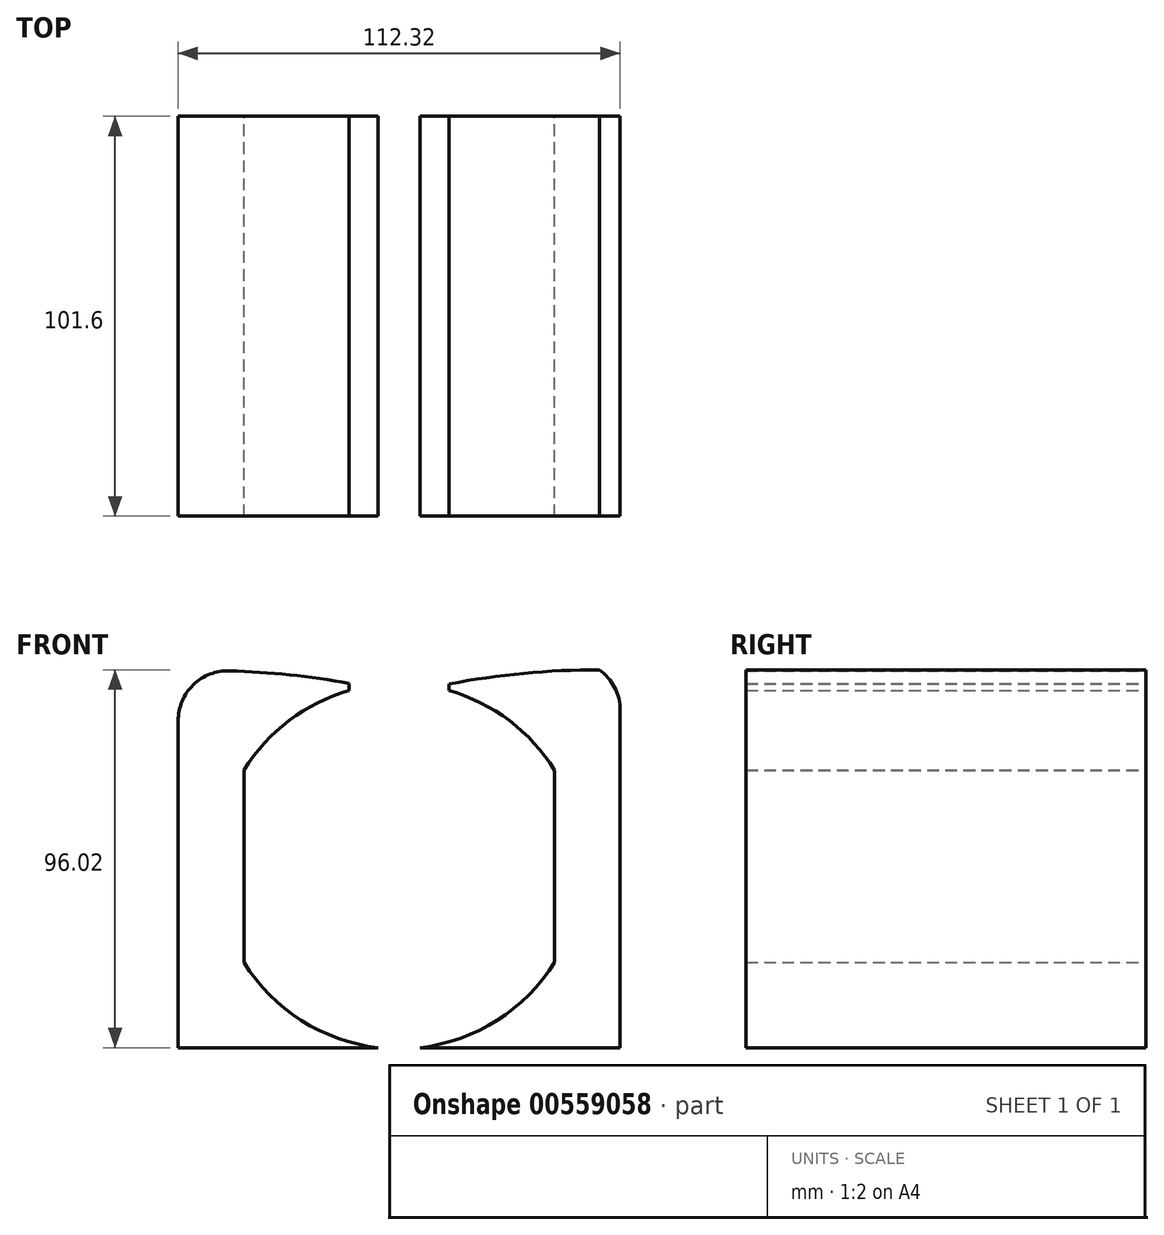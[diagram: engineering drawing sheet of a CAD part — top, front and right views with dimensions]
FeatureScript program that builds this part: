
annotation { "Feature Type Name" : "Feature", "Feature Type Description" : "" }
export const myFeature = defineFeature(function(context is Context, id is Id, definition is map)
    precondition{}
    {
        {
            var Q0;
            Q0=qCreatedBy(makeId("Front.planeOp"),FACE);
            var sketch = newSketch(context, id + "F0", { "sketchPlane" : qUnion([Q0])});
            skLineSegment(sketch, "E0.top", {"start": v(-56.16, -53.27) * mm, "end": v(-5.36, -53.27) * mm});
            skLineSegment(sketch, "E0.left", {"start": v(-56.16, 29.78) * mm, "end": v(-56.16, -53.27) * mm});
            skLineSegment(sketch, "E0.right", {"start": v(-12.7, 39.28) * mm, "end": v(-12.7, 37.44) * mm});
            skLineSegment(sketch, "E1.top", {"start": v(5.36, -53.27) * mm, "end": v(56.16, -53.27) * mm});
            skLineSegment(sketch, "E1.left", {"start": v(12.7, 39.14) * mm, "end": v(12.7, 37.44) * mm});
            skLineSegment(sketch, "E1.right", {"start": v(56.16, 32.42) * mm, "end": v(56.16, -53.27) * mm});
            skPoint(sketch, "E2.visualSharp", {"position": v(-56.16, 42.06) * mm});
            skArc(sketch, "E2.filletArc", {"start": v(-43.08, 42.48) * mm, "mid": v(-52.3, 38.9) * mm, "end": v(-56.16, 29.78) * mm});
            skPoint(sketch, "E3.visualSharp", {"position": v(56.16, 42.06) * mm});
            skArc(sketch, "E3.filletArc", {"start": v(56.16, 32.42) * mm, "mid": v(54.75, 38.23) * mm, "end": v(50.83, 42.75) * mm});
            skArc(sketch, "E4", {"start": v(5.36, -53.27) * mm, "mid": v(24.9, -46.34) * mm, "end": v(39.46, -31.58) * mm});
            skArc(sketch, "E5", {"start": v(39.46, 17.21) * mm, "mid": v(27.97, 29.83) * mm, "end": v(12.7, 37.44) * mm});
            skArc(sketch, "E6.trimOffspring", {"start": v(-12.7, 37.44) * mm, "mid": v(-27.95, 29.85) * mm, "end": v(-39.43, 17.27) * mm});
            skLineSegment(sketch, "E7", {"start": v(-39.43, 17.27) * mm, "end": v(-39.43, -31.64) * mm});
            skLineSegment(sketch, "E8", {"start": v(39.46, 17.21) * mm, "end": v(39.46, -31.58) * mm});
            skArc(sketch, "E9.trimOffspring", {"start": v(-39.43, -31.64) * mm, "mid": v(-24.87, -46.35) * mm, "end": v(-5.36, -53.27) * mm});
            skPoint(sketch, "E10.orphan", {"position": v(45.84, 0) * mm});
            skArc(sketch, "E11", {"start": v(-12.7, 39.28) * mm, "mid": v(-27.83, 41.45) * mm, "end": v(-43.08, 42.48) * mm});
            skArc(sketch, "E12", {"start": v(50.83, 42.75) * mm, "mid": v(31.68, 41.85) * mm, "end": v(12.7, 39.14) * mm});
            skPoint(sketch, "E13.orphan", {"position": v(-12.7, 42.06) * mm});
            skPoint(sketch, "E14.orphan", {"position": v(-43.08, 39.86) * mm});
            skPoint(sketch, "E15.end.orphan", {"position": v(50.83, 39.68) * mm});
            skSolve(sketch);
        }
        {
            var Q0;
            Q0=makeQuery(id+"F0.imprint","IMPRINT",FACE,{"disambiguationData":[TD([[makeQuery(id+"F0.imprint","IMPRINT",EDGE,{"derivedFrom":sQuery(id+"F0.wireOp",EDGE,"E0.top")}),1.0]])]});
            var Q1;
            Q1=makeQuery(id+"F0.imprint","IMPRINT",FACE,{"disambiguationData":[TD([[makeQuery(id+"F0.imprint","IMPRINT",EDGE,{"derivedFrom":sQuery(id+"F0.wireOp",EDGE,"E1.top")}),1.0]])]});
            extrude(context, id + "F1", {"entities" : qUnion([Q0, Q1]), "endBound" : BoundingType.SYMMETRIC, "depth" : 101.6 * mm, "offsetDistance" : 25.4 * mm});
        }
    });
